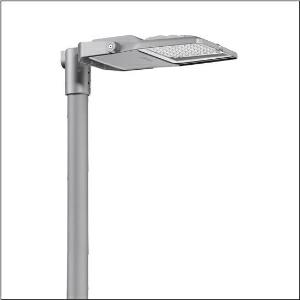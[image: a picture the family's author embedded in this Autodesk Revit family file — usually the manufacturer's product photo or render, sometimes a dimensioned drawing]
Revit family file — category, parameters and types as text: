
# Revit family: floodlight_fl_21_iq_mini___pl52_5xa7772b4d3a_2373
name_source: partatom
category: Lighting Fixtures
units: mm (PartAtom-declared; Revit-internal decimal feet)

## family parameters
Cut with Voids When Loaded = No
Host = Face
Light Source = No
Part Type = Normal
Room Calculation Point = No
Round Connector Dimension = Use Diameter
Shared = No

## types (1)
- --- (1 x LED, 6490 lm, 45.5 W, 4000K)
    Apparent Load = 46 VA
    CIE Flux Codes = 26 60 98 100 100
    Color Rendering = 70
    Color Temperature = 4000K
    Default Elevation = 1800 mm
    Description = Floodlight FL 21 iQ mini, floodlight, primary light control with lens, of PMMA, primary optical cover: protective disc, of toughened safety glass, transparent, light distribution: PL52, light emission: direct distribution, installation type: surface-mounted, LED, High Power LED, rated luminous flux: 6.490lm, luminous efficacy: 143lm/W, light colour: 740, colour temperature: 4000K, control: Auto-Match, Temp-Guard, Night-Set, Smart-Wire, Desk-Remote (wireless, voltage-free reading and setting of iQ features in the workshop via application-optimized NFC function/RFID function), optimised constant luminous flux control (CLO 2.0), Light-Fading, Lumen-Switch, with terminal, 6-pole, mains connection: 220..240V, AC, 50/60Hz, start of lifetime: 46W, end of service life: 48W, reduction: 22W, luminaire housing, of diecast aluminium, powder-coated, Siteco® metallic grey (DB 702S), corrosivity category C5 mid according to DIN EN ISO 12944, sealing non-destructively replaceable, please order mast flange separately, mast bracket, of steel, galvanised, powder-coated, protection rating (complete): IP66, insulation class (complete): insulation class II (safety insulation), certification: CE, ENEC, VDE, protection symbol: D, impact resistance: IK08, permissible operating ambient temperature: -40..+40°C, permissible operating ambient temperature for outdoor applications: -40..+50°C, standard: DIN EN 12944, LABS conformity tested according to VDMA 24364:2018-05, packaging unit: 1 piece

Light Distribution: PL52
    Height = 70 mm
    Lamp = 1 x LED
    Lamp Light Flux = 6490 lm
    Lamp Power = 45.5 W
    Lamp count = 1
    Length = 485 mm
    Luminous efficacy = 143 lm/W
    Manufacturer = Siteco
    ModVariant = No
    Model = 5XA7772B4D3A
    Number of Poles = 1
    OnlyDefault = Yes
    Power Factor = 1
    Product Name = Floodlight FL 21 iQ mini | PL52
    Product group = floodlight | pylon annexe
    ProductGroupID = 6200
    Protection Class = Protection class II
    Protection Degree = IP 66
    RLX_Detail_Level = 1
    RLX_Emergency_Light_Flux = 0 lm
    RLX_Emergency_Type = 0
    RLX_Emergency_Type_DB = No
    RlxData = <blob elided: 101401 chars, md5=04b9833f>
    Socket = socket
    Standby Power = 0 W
    System Light Flux = 6490 lm
    System Power = 46 W
    Type Comments = factory setting: luminous flux: 100 % | dim-lin: 254 | 463 mA
    Type Image = l_1007125.jpg
    URL = http://relux.com
    VarID = @adj_114851
    Voltage = 0 V
    Weight = 0.00 kg
    Width = 337 mm

## geometry (parser evidence)
native form markers: Blend x4, Sweep x12
no freeform markers — native parametric forms only
